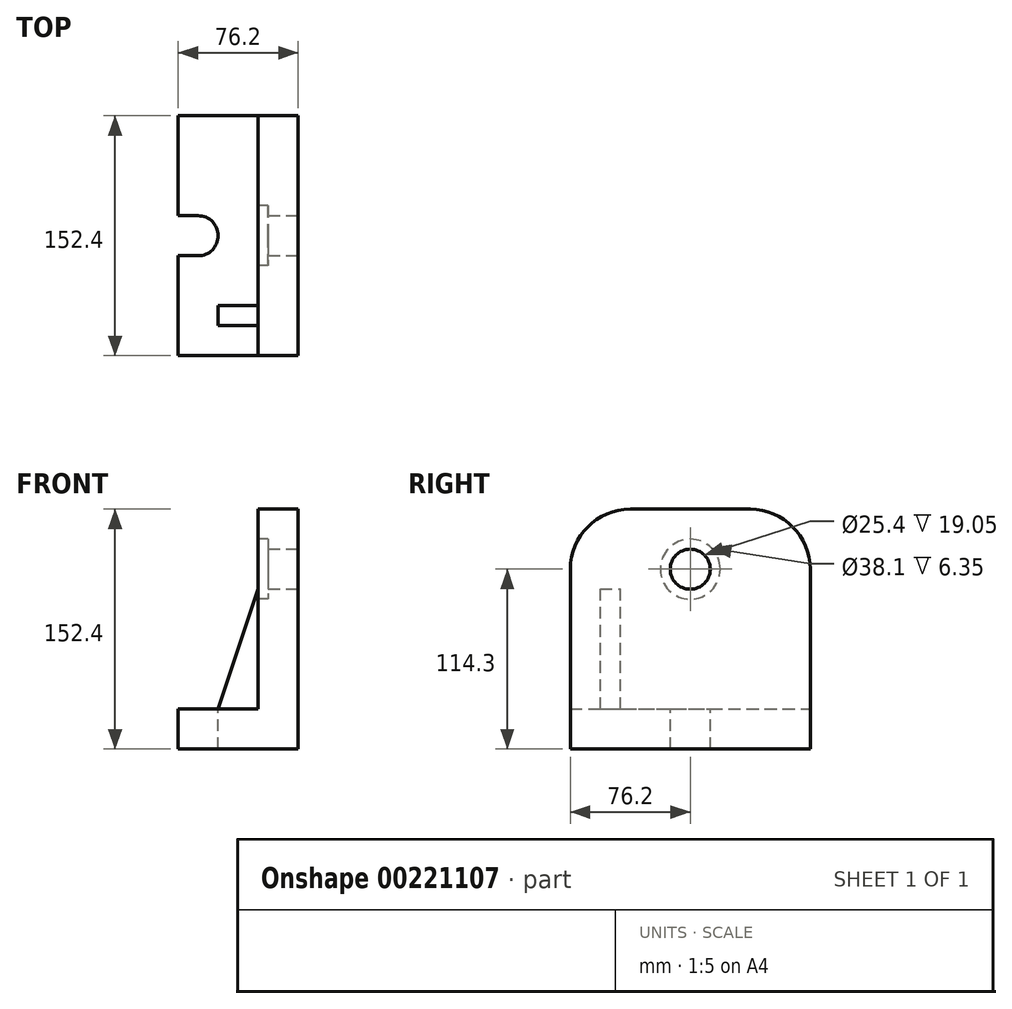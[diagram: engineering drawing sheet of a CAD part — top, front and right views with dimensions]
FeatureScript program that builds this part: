
annotation { "Feature Type Name" : "Feature", "Feature Type Description" : "" }
export const myFeature = defineFeature(function(context is Context, id is Id, definition is map)
    precondition{}
    {
        {
            var Q0;
            Q0=qCreatedBy(makeId("Front.planeOp"),FACE);
            var sketch = newSketch(context, id + "F0", { "sketchPlane" : qUnion([Q0])});
            skLineSegment(sketch, "E0", {"start": v(0, 152.4) * mm, "end": v(0, 0) * mm});
            skLineSegment(sketch, "E1", {"start": v(0, 0) * mm, "end": v(-76.2, 0) * mm});
            skLineSegment(sketch, "E2", {"start": v(-76.2, 0) * mm, "end": v(-76.2, 25.4) * mm});
            skLineSegment(sketch, "E3", {"start": v(-76.2, 25.4) * mm, "end": v(-25.4, 25.4) * mm});
            skLineSegment(sketch, "E4", {"start": v(-25.4, 25.4) * mm, "end": v(-25.4, 152.4) * mm});
            skLineSegment(sketch, "E5", {"start": v(-25.4, 152.4) * mm, "end": v(0, 152.4) * mm});
            skSolve(sketch);
        }
        {
            var Q0;
            Q0 = qSketchRegion(id + "F0", true);
            extrude(context, id + "F1", {"entities" : qUnion([Q0]), "endBound" : BoundingType.SYMMETRIC, "depth" : 152.4 * mm});
        }
        {
            var Q0;
            Q0=makeQuery(id+"F1.opExtrude","SWEPT_FACE",FACE,{"disambiguationData":[OSD([sQuery(id+"F0.wireOp",EDGE,"E0")])]});
            var sketch = newSketch(context, id + "F2", { "sketchPlane" : qUnion([Q0])});
            skLineSegment(sketch, "E6", {"start": v(0, 0) * mm, "end": v(0, 114.3) * mm, "construction": true});
            skCircle(sketch, "E7", {"center": v(0, 114.3) * mm, "radius": 12.7 * mm});
            skSolve(sketch);
        }
        {
            var Q0;
            Q0 = qSketchRegion(id + "F2", true);
            extrude(context, id + "F3", {"entities" : qUnion([Q0]), "operationType" : NewBodyOperationType.REMOVE, "endBound" : BoundingType.THROUGH_ALL, "oppositeDirection" : true, "depth" : 25.4 * mm});
        }
        {
            var Q0;
            Q0=makeQuery(id+"F1.opExtrude","SWEPT_FACE",FACE,{"disambiguationData":[OSD([sQuery(id+"F0.wireOp",EDGE,"E3")])]});
            var sketch = newSketch(context, id + "F4", { "sketchPlane" : qUnion([Q0])});
            skLineSegment(sketch, "E8", {"start": v(-76.2, 0) * mm, "end": v(-55.9, 0) * mm, "construction": true});
            skPoint(sketch, "E8.endSnap0", {"position": v(-76.2, 0) * mm});
            skLineSegment(sketch, "E9.0", {"start": v(-76.2, -12.7) * mm, "end": v(-63.5, -12.7) * mm});
            skLineSegment(sketch, "E10.0", {"start": v(-76.2, 12.7) * mm, "end": v(-63.5, 12.7) * mm});
            skArc(sketch, "E11", {"start": v(-63.5, -12.7) * mm, "mid": v(-50.8, 0) * mm, "end": v(-63.5, 12.7) * mm});
            skLineSegment(sketch, "E12", {"start": v(-76.2, -12.7) * mm, "end": v(-76.2, 12.7) * mm});
            skSolve(sketch);
        }
        {
            var Q0;
            Q0 = qSketchRegion(id + "F4", true);
            extrude(context, id + "F5", {"entities" : qUnion([Q0]), "operationType" : NewBodyOperationType.REMOVE, "endBound" : BoundingType.THROUGH_ALL, "oppositeDirection" : true, "depth" : 25.4 * mm});
        }
        {
            var Q0;
            Q0=makeQuery(id+"F1.opExtrude","SWEPT_FACE",FACE,{"disambiguationData":[OSD([sQuery(id+"F0.wireOp",EDGE,"E4")])]});
            var sketch = newSketch(context, id + "F6", { "sketchPlane" : qUnion([Q0])});
            skLineSegment(sketch, "E13.0", {"start": v(-76.2, 25.4) * mm, "end": v(-76.2, 152.4) * mm});
            skLineSegment(sketch, "E14.0", {"start": v(76.2, 152.4) * mm, "end": v(-76.2, 152.4) * mm});
            skLineSegment(sketch, "E15.0.0", {"start": v(-76.2, 114.3) * mm, "end": v(-76.2, 25.4) * mm});
            skLineSegment(sketch, "E15.0.1", {"start": v(-76.2, 25.4) * mm, "end": v(76.2, 25.4) * mm});
            skLineSegment(sketch, "E15.0.2", {"start": v(76.2, 25.4) * mm, "end": v(76.2, 114.3) * mm});
            skLineSegment(sketch, "E15.0.3", {"start": v(38.1, 152.4) * mm, "end": v(-38.1, 152.4) * mm});
            skPoint(sketch, "E16.visualSharp", {"position": v(-76.2, 152.4) * mm});
            skArc(sketch, "E16.filletArc", {"start": v(-38.1, 152.4) * mm, "mid": v(-65.04, 141.24) * mm, "end": v(-76.2, 114.3) * mm});
            skPoint(sketch, "E17.visualSharp", {"position": v(76.2, 152.4) * mm});
            skArc(sketch, "E17.filletArc", {"start": v(76.2, 114.3) * mm, "mid": v(65.04, 141.24) * mm, "end": v(38.1, 152.4) * mm});
            skSolve(sketch);
        }
        {
            var Q0;
            {var subQ0=sQuery(id+"F6.wireOp",EDGE,"E13.0");Q0=makeQuery(id+"F6.imprint","IMPRINT",FACE,{"disambiguationData":[TD([[makeQuery(id+"F6.imprint","IMPRINT",EDGE,{"derivedFrom":subQ0}),-1.0]])]});}
            var Q1;
            {var subQ3=sQuery(id+"F6.wireOp",EDGE,"E17.filletArc");Q1=makeQuery(id+"F6.imprint","IMPRINT",FACE,{"disambiguationData":[TD([[makeQuery(id+"F6.imprint","IMPRINT",EDGE,{"derivedFrom":subQ3}),-1.0]])]});}
            extrude(context, id + "F7", {"entities" : qUnion([Q0, Q1]), "operationType" : NewBodyOperationType.REMOVE, "endBound" : BoundingType.THROUGH_ALL, "oppositeDirection" : true, "depth" : 25.4 * mm});
        }
        {
            var Q0;
            Q0=makeQuery(id+"F1.opExtrude","SWEPT_FACE",FACE,{"disambiguationData":[OSD([sQuery(id+"F0.wireOp",EDGE,"E4")])]});
            var sketch = newSketch(context, id + "F8", { "sketchPlane" : qUnion([Q0])});
            skCircle(sketch, "E18", {"center": v(0, 114.3) * mm, "radius": 19.05 * mm});
            skCircle(sketch, "E19.0", {"center": v(0, 114.3) * mm, "radius": 12.7 * mm});
            skSolve(sketch);
        }
        {
            var Q0;
            Q0 = qSketchRegion(id + "F8", true);
            extrude(context, id + "F9", {"entities" : qUnion([Q0]), "operationType" : NewBodyOperationType.REMOVE, "oppositeDirection" : true, "depth" : 6.35 * mm});
        }
        {
            var Q0;
            Q0=qCreatedBy(makeId("Front.planeOp"),FACE);
            cPlane(context, id + "F10", {"entities" : qUnion([Q0]), "cplaneType" : CPlaneType.OFFSET, "offset" : 44.45 * mm, "width" : 152.4 * mm, "height" : 152.4 * mm});
        }
        {
            var Q0;
            Q0=qCreatedBy(id+"F10.planeOp",FACE);
            var sketch = newSketch(context, id + "F11", { "sketchPlane" : qUnion([Q0])});
            skLineSegment(sketch, "E20.0", {"start": v(-76.2, 25.4) * mm, "end": v(-25.4, 25.4) * mm});
            skLineSegment(sketch, "E20.1", {"start": v(-25.4, 25.4) * mm, "end": v(-25.4, 101.6) * mm});
            skLineSegment(sketch, "E21", {"start": v(-25.4, 101.6) * mm, "end": v(-50.8, 25.4) * mm});
            skSolve(sketch);
        }
        {
            var Q0;
            Q0 = qSketchRegion(id + "F11", true);
            extrude(context, id + "F12", {"entities" : qUnion([Q0]), "operationType" : NewBodyOperationType.ADD, "depth" : 12.7 * mm});
        }
    });
